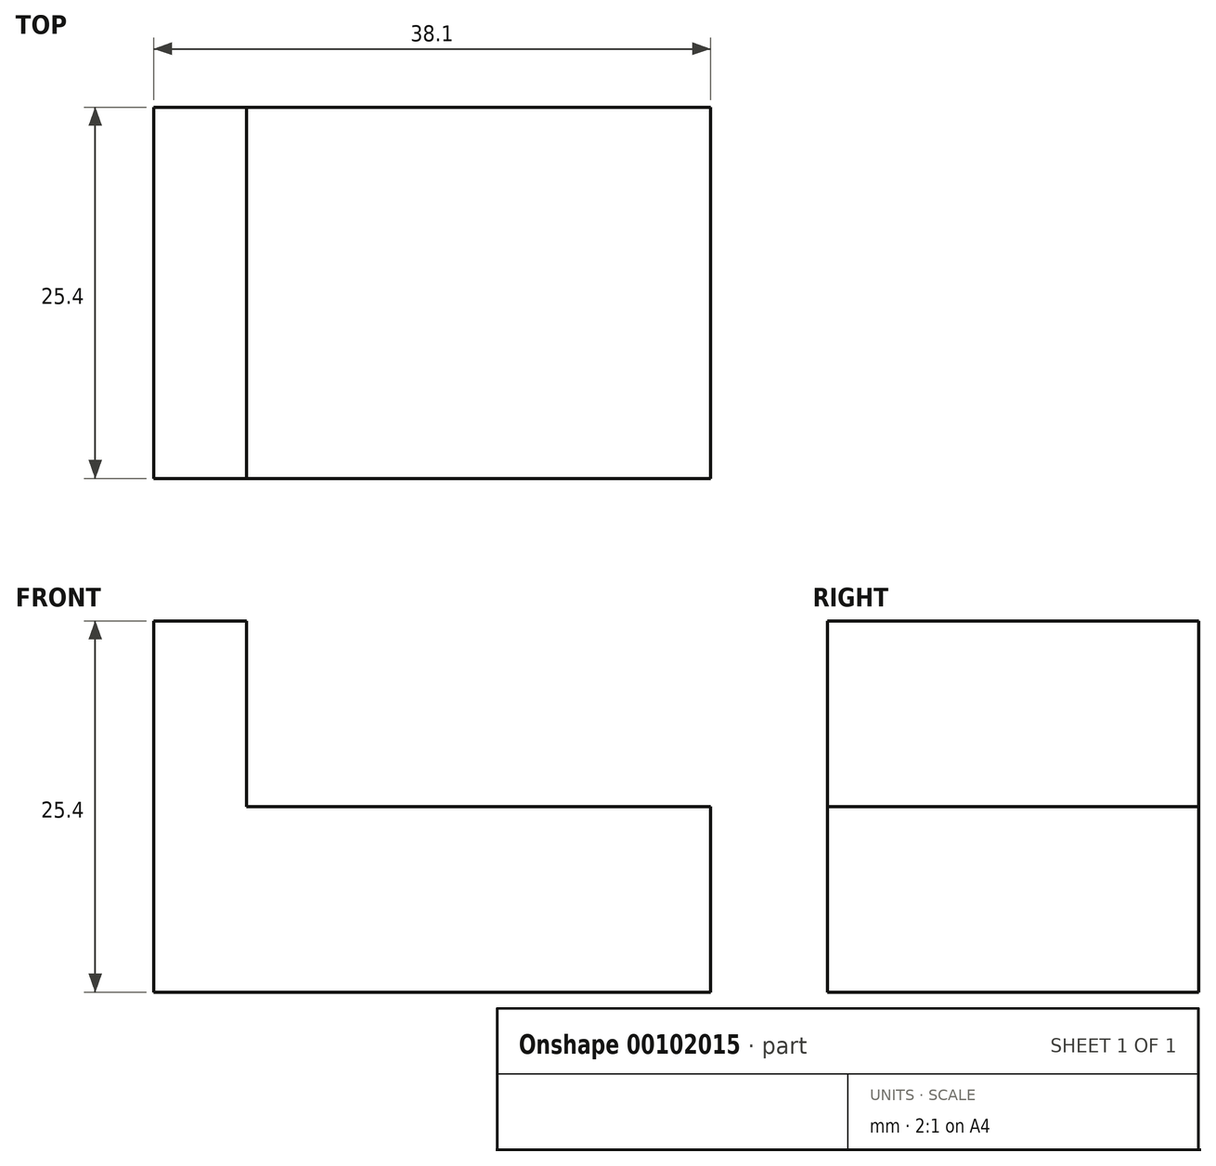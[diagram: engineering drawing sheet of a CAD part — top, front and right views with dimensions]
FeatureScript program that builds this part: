
annotation { "Feature Type Name" : "Feature", "Feature Type Description" : "" }
export const myFeature = defineFeature(function(context is Context, id is Id, definition is map)
    precondition{}
    {
        {
            var Q0;
            Q0=qCreatedBy(makeId("Front.planeOp"),FACE);
            var sketch = newSketch(context, id + "F0", { "sketchPlane" : qUnion([Q0])});
            skLineSegment(sketch, "E0.bottom", {"start": v(0, 0) * mm, "end": v(38.1, 0) * mm});
            skLineSegment(sketch, "E0.right", {"start": v(38.1, 0) * mm, "end": v(38.1, 12.7) * mm});
            skLineSegment(sketch, "E1", {"start": v(38.1, 12.7) * mm, "end": v(6.35, 12.7) * mm});
            skLineSegment(sketch, "E2", {"start": v(6.35, 12.7) * mm, "end": v(6.35, 25.4) * mm});
            skLineSegment(sketch, "E3", {"start": v(6.35, 25.4) * mm, "end": v(0, 25.4) * mm});
            skLineSegment(sketch, "E4", {"start": v(0, 25.4) * mm, "end": v(0, 0) * mm});
            skSolve(sketch);
        }
        {
            var Q0;
            Q0 = qSketchRegion(id + "F0", true);
            extrude(context, id + "F1", {"entities" : qUnion([Q0]), "endBound" : BoundingType.SYMMETRIC, "depth" : 25.4 * mm});
        }
    });
